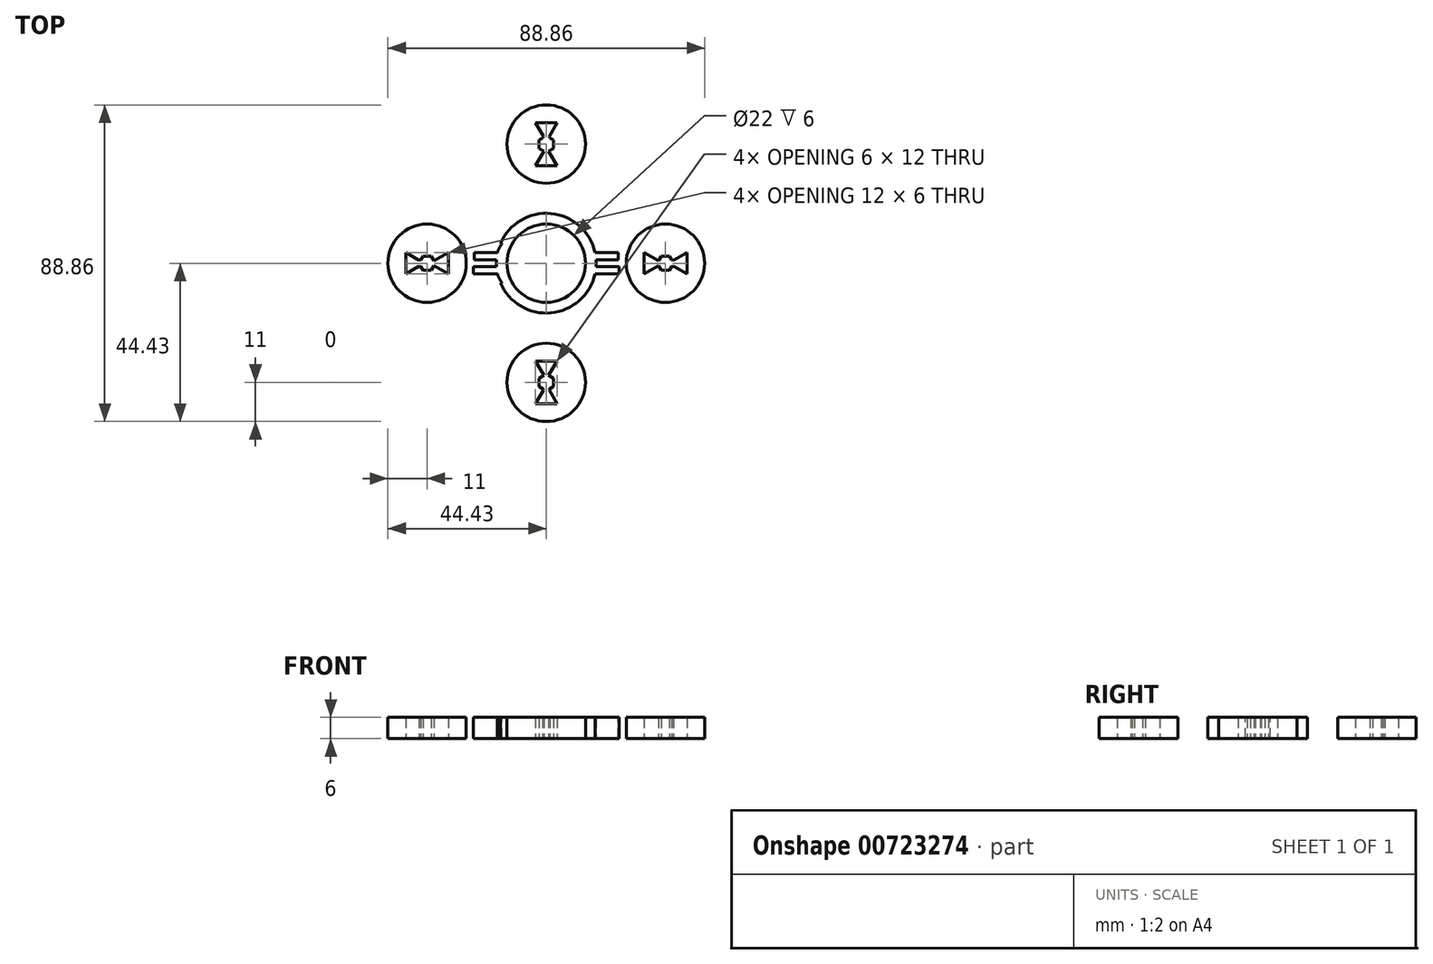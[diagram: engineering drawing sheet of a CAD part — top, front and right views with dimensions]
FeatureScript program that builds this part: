
annotation { "Feature Type Name" : "Feature", "Feature Type Description" : "" }
export const myFeature = defineFeature(function(context is Context, id is Id, definition is map)
    precondition{}
    {
        {
            var Q0;
            Q0=qCreatedBy(makeId("Top.planeOp"),FACE);
            var sketch = newSketch(context, id + "F0", { "sketchPlane" : qUnion([Q0])});
            skCircle(sketch, "E0", {"center": v(0, 0) * mm, "radius": 11 * mm});
            skCircle(sketch, "E1", {"center": v(0, 0) * mm, "radius": 14 * mm});
            skLineSegment(sketch, "E2", {"start": v(-5.2, 13) * mm, "end": v(-37.7, 0) * mm});
            skLineSegment(sketch, "E3", {"start": v(-37.7, 0) * mm, "end": v(-5.2, -13) * mm});
            skCircle(sketch, "E4", {"center": v(-33.43, 0) * mm, "radius": 11 * mm});
            skCircle(sketch, "E5.cCircle", {"center": v(-37.7, 0) * mm, "radius": 1.73 * mm, "construction": true});
            skLineSegment(sketch, "E5.0", {"start": v(-39.43, -3) * mm, "end": v(-39.43, 3) * mm});
            skLineSegment(sketch, "E5.1", {"start": v(-39.43, 3) * mm, "end": v(-35.34, 0.64) * mm});
            skLineSegment(sketch, "E5.2", {"start": v(-35.34, -0.64) * mm, "end": v(-39.43, -3) * mm});
            skPoint(sketch, "E5.0.midPoint", {"position": v(-39.43, 0) * mm});
            skCircle(sketch, "E6.cCircle", {"center": v(-29.16, 0) * mm, "radius": 1.73 * mm, "construction": true});
            skLineSegment(sketch, "E6.0", {"start": v(-27.43, 3) * mm, "end": v(-27.43, -3) * mm});
            skLineSegment(sketch, "E6.1", {"start": v(-27.43, -3) * mm, "end": v(-31.52, -0.64) * mm});
            skLineSegment(sketch, "E6.2", {"start": v(-31.52, 0.64) * mm, "end": v(-27.43, 3) * mm});
            skArc(sketch, "E7.cCircle", {"start": v(-31.52, 0.64) * mm, "mid": v(-33.43, 2.02) * mm, "end": v(-35.34, 0.64) * mm, "construction": true});
            skLineSegment(sketch, "E7.0", {"start": v(-35.17, 1) * mm, "end": v(-34.6, 2.02) * mm});
            skLineSegment(sketch, "E7.1", {"start": v(-34.6, 2.02) * mm, "end": v(-32.26, 2.02) * mm});
            skLineSegment(sketch, "E7.2", {"start": v(-32.26, 2.02) * mm, "end": v(-31.48, 0.66) * mm});
            skLineSegment(sketch, "E7.3", {"start": v(-31.48, -0.66) * mm, "end": v(-32.26, -2.02) * mm});
            skLineSegment(sketch, "E7.4", {"start": v(-32.26, -2.02) * mm, "end": v(-34.6, -2.02) * mm});
            skLineSegment(sketch, "E7.5", {"start": v(-34.6, -2.02) * mm, "end": v(-35.38, -0.66) * mm});
            skPoint(sketch, "E7.0.midPoint", {"position": v(-35.17, 1) * mm});
            skPoint(sketch, "E8.orphan", {"position": v(-31.1, 0) * mm});
            skPoint(sketch, "E9.orphan", {"position": v(-35.76, 0) * mm});
            skArc(sketch, "E10.trimOffspring", {"start": v(-35.34, -0.64) * mm, "mid": v(-33.43, -2.02) * mm, "end": v(-31.52, -0.64) * mm, "construction": true});
            skPoint(sketch, "E11.orphan", {"position": v(-34.23, 0) * mm});
            skPoint(sketch, "E12.orphan", {"position": v(-32.62, 0) * mm});
            skLineSegment(sketch, "E13", {"start": v(-35.8, 2.02) * mm, "end": v(-27.43, 2.02) * mm, "construction": true});
            skLineSegment(sketch, "E14.MirrorCS", {"start": v(35.17, 1) * mm, "end": v(34.6, 2.02) * mm});
            skLineSegment(sketch, "E15.MirrorCS", {"start": v(31.48, -0.66) * mm, "end": v(32.26, -2.02) * mm});
            skLineSegment(sketch, "E16.MirrorCS", {"start": v(32.26, 2.02) * mm, "end": v(31.48, 0.66) * mm});
            skLineSegment(sketch, "E17.MirrorCS", {"start": v(34.6, -2.02) * mm, "end": v(35.38, -0.66) * mm});
            skLineSegment(sketch, "E18.MirrorCS", {"start": v(32.26, -2.02) * mm, "end": v(34.6, -2.02) * mm});
            skLineSegment(sketch, "E19.MirrorCS", {"start": v(34.6, 2.02) * mm, "end": v(32.26, 2.02) * mm});
            skArc(sketch, "E20.MirrorCS", {"start": v(35.34, -0.64) * mm, "mid": v(33.43, -2.02) * mm, "end": v(31.52, -0.64) * mm, "construction": true});
            skLineSegment(sketch, "E21.MirrorCS", {"start": v(39.43, -3) * mm, "end": v(39.43, 3) * mm});
            skArc(sketch, "E22.MirrorCS", {"start": v(31.52, 0.64) * mm, "mid": v(33.43, 2.02) * mm, "end": v(35.34, 0.64) * mm, "construction": true});
            skLineSegment(sketch, "E23.MirrorCS", {"start": v(35.8, 2.02) * mm, "end": v(27.43, 2.02) * mm, "construction": true});
            skLineSegment(sketch, "E24.MirrorCS", {"start": v(31.52, 0.64) * mm, "end": v(27.43, 3) * mm});
            skLineSegment(sketch, "E25.MirrorCS", {"start": v(35.34, -0.64) * mm, "end": v(39.43, -3) * mm});
            skLineSegment(sketch, "E26.MirrorCS", {"start": v(39.43, 3) * mm, "end": v(35.34, 0.64) * mm});
            skLineSegment(sketch, "E27.MirrorCS", {"start": v(27.43, -3) * mm, "end": v(31.52, -0.64) * mm});
            skCircle(sketch, "E28.MirrorC", {"center": v(37.7, 0) * mm, "radius": 1.73 * mm, "construction": true});
            skLineSegment(sketch, "E29.MirrorCS", {"start": v(27.43, 3) * mm, "end": v(27.43, -3) * mm});
            skCircle(sketch, "E30.MirrorC", {"center": v(29.16, 0) * mm, "radius": 1.73 * mm, "construction": true});
            skPoint(sketch, "E31.MirrorP", {"position": v(35.76, 0) * mm});
            skPoint(sketch, "E32.MirrorP", {"position": v(39.43, 0) * mm});
            skPoint(sketch, "E33.MirrorP", {"position": v(35.17, 1) * mm});
            skPoint(sketch, "E34.MirrorP", {"position": v(31.1, 0) * mm});
            skCircle(sketch, "E35.MirrorC", {"center": v(33.43, 0) * mm, "radius": 11 * mm});
            skLineSegment(sketch, "E36.MirrorCS", {"start": v(5.2, 13) * mm, "end": v(37.7, 0) * mm});
            skLineSegment(sketch, "E37.MirrorCS", {"start": v(37.7, 0) * mm, "end": v(5.2, -13) * mm});
            skPoint(sketch, "E38.MirrorP", {"position": v(34.23, 0) * mm});
            skPoint(sketch, "E39.MirrorP", {"position": v(32.62, 0) * mm});
            skSolve(sketch);
        }
        {
            var Q0;
            Q0 = qSketchRegion(id + "F0", true);
            extrude(context, id + "F1", {"entities" : qUnion([Q0]), "depth" : 6 * mm, "offsetDistance" : 25 * mm});
        }
        {
            var Q0;
            Q0=makeQuery(id+"F1.opExtrude","CAP_FACE",FACE,{"disambiguationData":[OSD([sQuery(id+"F0.wireOp",EDGE,"E0"),sQuery(id+"F0.wireOp",EDGE,"E1"),sQuery(id+"F0.wireOp",EDGE,"E2"),sQuery(id+"F0.wireOp",EDGE,"E3"),sQuery(id+"F0.wireOp",EDGE,"E4"),sQuery(id+"F0.wireOp",EDGE,"E5.0"),sQuery(id+"F0.wireOp",EDGE,"E5.1"),sQuery(id+"F0.wireOp",EDGE,"E5.2"),sQuery(id+"F0.wireOp",EDGE,"E6.0"),sQuery(id+"F0.wireOp",EDGE,"E6.1"),sQuery(id+"F0.wireOp",EDGE,"E6.2"),sQuery(id+"F0.wireOp",EDGE,"E7.0"),sQuery(id+"F0.wireOp",EDGE,"E7.1"),sQuery(id+"F0.wireOp",EDGE,"E7.2"),sQuery(id+"F0.wireOp",EDGE,"E7.3"),sQuery(id+"F0.wireOp",EDGE,"E7.4"),sQuery(id+"F0.wireOp",EDGE,"E7.5")])],"isStart":false});
            var sketch = newSketch(context, id + "F2", { "sketchPlane" : qUnion([Q0])});
            skLineSegment(sketch, "E40.bottom", {"start": v(-18.36, 5.51) * mm, "end": v(-13.84, 5.51) * mm});
            skLineSegment(sketch, "E40.top", {"start": v(-18.36, -5.51) * mm, "end": v(-13.84, -5.51) * mm});
            skArc(sketch, "E41", {"start": v(-12.43, 5.51) * mm, "mid": v(-14.24, 0) * mm, "end": v(-12.43, -5.51) * mm});
            skLineSegment(sketch, "E42", {"start": v(-13.84, 5.51) * mm, "end": v(-12.43, 5.51) * mm});
            skLineSegment(sketch, "E43", {"start": v(-13.84, -5.51) * mm, "end": v(-12.43, -5.51) * mm});
            skArc(sketch, "E44", {"start": v(-18.36, 5.51) * mm, "mid": v(-20.16, 0) * mm, "end": v(-18.36, -5.51) * mm});
            skArc(sketch, "E45.MirrorCS", {"start": v(18.36, 5.51) * mm, "mid": v(20.16, 0) * mm, "end": v(18.36, -5.51) * mm});
            skLineSegment(sketch, "E46.MirrorCS", {"start": v(18.36, -5.51) * mm, "end": v(13.84, -5.51) * mm});
            skLineSegment(sketch, "E47.MirrorCS", {"start": v(18.36, 5.51) * mm, "end": v(13.84, 5.51) * mm});
            skArc(sketch, "E48.MirrorCS", {"start": v(12.43, 5.51) * mm, "mid": v(14.24, 0) * mm, "end": v(12.43, -5.51) * mm});
            skLineSegment(sketch, "E49.MirrorCS", {"start": v(13.84, -5.51) * mm, "end": v(12.43, -5.51) * mm});
            skLineSegment(sketch, "E50.MirrorCS", {"start": v(13.84, 5.51) * mm, "end": v(12.43, 5.51) * mm});
            skSolve(sketch);
        }
        {
            var Q0;
            Q0=makeQuery(id+"F2.imprint","IMPRINT",FACE,{"disambiguationData":[TD([[makeQuery(id+"F2.imprint","IMPRINT",EDGE,{"derivedFrom":sQuery(id+"F2.wireOp",EDGE,"E40.bottom")}),-1.0]])]});
            var Q1;
            Q1=makeQuery(id+"F2.imprint","IMPRINT",FACE,{"disambiguationData":[TD([[makeQuery(id+"F2.imprint","IMPRINT",EDGE,{"derivedFrom":sQuery(id+"F2.wireOp",EDGE,"E45.MirrorCS")}),-1.0]])]});
            extrude(context, id + "F3", {"entities" : qUnion([Q0, Q1]), "operationType" : NewBodyOperationType.REMOVE, "oppositeDirection" : true, "depth" : 25 * mm, "offsetDistance" : 25 * mm});
        }
        {
            var Q0;
            Q0=makeQuery(id+"F1.opExtrude","CAP_FACE",FACE,{"disambiguationData":[OSD([sQuery(id+"F0.wireOp",EDGE,"E0"),sQuery(id+"F0.wireOp",EDGE,"E1"),sQuery(id+"F0.wireOp",EDGE,"E2"),sQuery(id+"F0.wireOp",EDGE,"E3"),sQuery(id+"F0.wireOp",EDGE,"E4"),sQuery(id+"F0.wireOp",EDGE,"E5.0"),sQuery(id+"F0.wireOp",EDGE,"E5.1"),sQuery(id+"F0.wireOp",EDGE,"E5.2"),sQuery(id+"F0.wireOp",EDGE,"E6.0"),sQuery(id+"F0.wireOp",EDGE,"E6.1"),sQuery(id+"F0.wireOp",EDGE,"E6.2"),sQuery(id+"F0.wireOp",EDGE,"E7.0"),sQuery(id+"F0.wireOp",EDGE,"E7.1"),sQuery(id+"F0.wireOp",EDGE,"E7.2"),sQuery(id+"F0.wireOp",EDGE,"E7.3"),sQuery(id+"F0.wireOp",EDGE,"E7.4"),sQuery(id+"F0.wireOp",EDGE,"E7.5")])],"isStart":false});
            var sketch = newSketch(context, id + "F4", { "sketchPlane" : qUnion([Q0])});
            skLineSegment(sketch, "E51.bottom", {"start": v(-20.4, -3.01) * mm, "end": v(-13.32, -3.01) * mm});
            skLineSegment(sketch, "E51.top", {"start": v(-20.4, -1.01) * mm, "end": v(-13.32, -1.01) * mm});
            skLineSegment(sketch, "E51.left", {"start": v(-20.4, -3.01) * mm, "end": v(-20.4, -1.01) * mm});
            skLineSegment(sketch, "E51.right", {"start": v(-13.32, -3.01) * mm, "end": v(-13.32, -1.01) * mm});
            skLineSegment(sketch, "E52.bottom", {"start": v(-20.23, 3.01) * mm, "end": v(-11.96, 3.01) * mm});
            skLineSegment(sketch, "E52.top", {"start": v(-20.23, 1.01) * mm, "end": v(-11.96, 1.01) * mm});
            skLineSegment(sketch, "E52.left", {"start": v(-20.23, 3.01) * mm, "end": v(-20.23, 1.01) * mm});
            skLineSegment(sketch, "E52.right", {"start": v(-11.96, 3.01) * mm, "end": v(-11.96, 1.01) * mm});
            skLineSegment(sketch, "E53.MirrorCS", {"start": v(20.23, 1.01) * mm, "end": v(11.96, 1.01) * mm});
            skLineSegment(sketch, "E54.MirrorCS", {"start": v(20.23, 3.01) * mm, "end": v(11.96, 3.01) * mm});
            skLineSegment(sketch, "E55.MirrorCS", {"start": v(20.4, -1.01) * mm, "end": v(13.32, -1.01) * mm});
            skLineSegment(sketch, "E56.MirrorCS", {"start": v(20.4, -3.01) * mm, "end": v(13.32, -3.01) * mm});
            skLineSegment(sketch, "E57.MirrorCS", {"start": v(20.4, -3.01) * mm, "end": v(20.4, -1.01) * mm});
            skLineSegment(sketch, "E58.MirrorCS", {"start": v(13.32, -3.01) * mm, "end": v(13.32, -1.01) * mm});
            skLineSegment(sketch, "E59.MirrorCS", {"start": v(11.96, 3.01) * mm, "end": v(11.96, 1.01) * mm});
            skLineSegment(sketch, "E60.MirrorCS", {"start": v(20.23, 3.01) * mm, "end": v(20.23, 1.01) * mm});
            skSolve(sketch);
        }
        {
            var Q0;
            Q0 = qSketchRegion(id + "F4", true);
            extrude(context, id + "F5", {"entities" : qUnion([Q0]), "operationType" : NewBodyOperationType.ADD, "oppositeDirection" : true, "depth" : 6 * mm, "offsetDistance" : 25 * mm});
        }
        {
            var Q0;
            Q0=makeQuery(id+"F1.opExtrude","SWEPT_BODY",BODY,{"disambiguationData":[OSD([sQuery(id+"F0.wireOp",EDGE,"E0"),sQuery(id+"F0.wireOp",EDGE,"E1"),sQuery(id+"F0.wireOp",EDGE,"E2"),sQuery(id+"F0.wireOp",EDGE,"E3"),sQuery(id+"F0.wireOp",EDGE,"E4"),sQuery(id+"F0.wireOp",EDGE,"E5.0"),sQuery(id+"F0.wireOp",EDGE,"E5.1"),sQuery(id+"F0.wireOp",EDGE,"E5.2"),sQuery(id+"F0.wireOp",EDGE,"E6.0"),sQuery(id+"F0.wireOp",EDGE,"E6.1"),sQuery(id+"F0.wireOp",EDGE,"E6.2"),sQuery(id+"F0.wireOp",EDGE,"E7.0"),sQuery(id+"F0.wireOp",EDGE,"E7.1"),sQuery(id+"F0.wireOp",EDGE,"E7.2"),sQuery(id+"F0.wireOp",EDGE,"E7.3"),sQuery(id+"F0.wireOp",EDGE,"E7.4"),sQuery(id+"F0.wireOp",EDGE,"E7.5"),sQuery(id+"F0.wireOp",EDGE,"E14.MirrorCS"),sQuery(id+"F0.wireOp",EDGE,"E15.MirrorCS"),sQuery(id+"F0.wireOp",EDGE,"E16.MirrorCS"),sQuery(id+"F0.wireOp",EDGE,"E17.MirrorCS"),sQuery(id+"F0.wireOp",EDGE,"E18.MirrorCS"),sQuery(id+"F0.wireOp",EDGE,"E19.MirrorCS"),sQuery(id+"F0.wireOp",EDGE,"E21.MirrorCS"),sQuery(id+"F0.wireOp",EDGE,"E24.MirrorCS"),sQuery(id+"F0.wireOp",EDGE,"E25.MirrorCS"),sQuery(id+"F0.wireOp",EDGE,"E26.MirrorCS"),sQuery(id+"F0.wireOp",EDGE,"E27.MirrorCS"),sQuery(id+"F0.wireOp",EDGE,"E29.MirrorCS"),sQuery(id+"F0.wireOp",EDGE,"E35.MirrorC"),sQuery(id+"F0.wireOp",EDGE,"E36.MirrorCS"),sQuery(id+"F0.wireOp",EDGE,"E37.MirrorCS")])]});
            var Q1;
            Q1=makeQuery(id+"F1.opExtrude","CAP_EDGE",EDGE,{"disambiguationData":[OSD([sQuery(id+"F0.wireOp",EDGE,"E0")])],"isStart":false});
            circularPattern(context, id + "F6", {"entities" : qUnion([Q0]), "axis" : qUnion([Q1]), "angle" : 360 * degree, "instanceCount" : 4, "equalSpace" : true});
        }
    });
